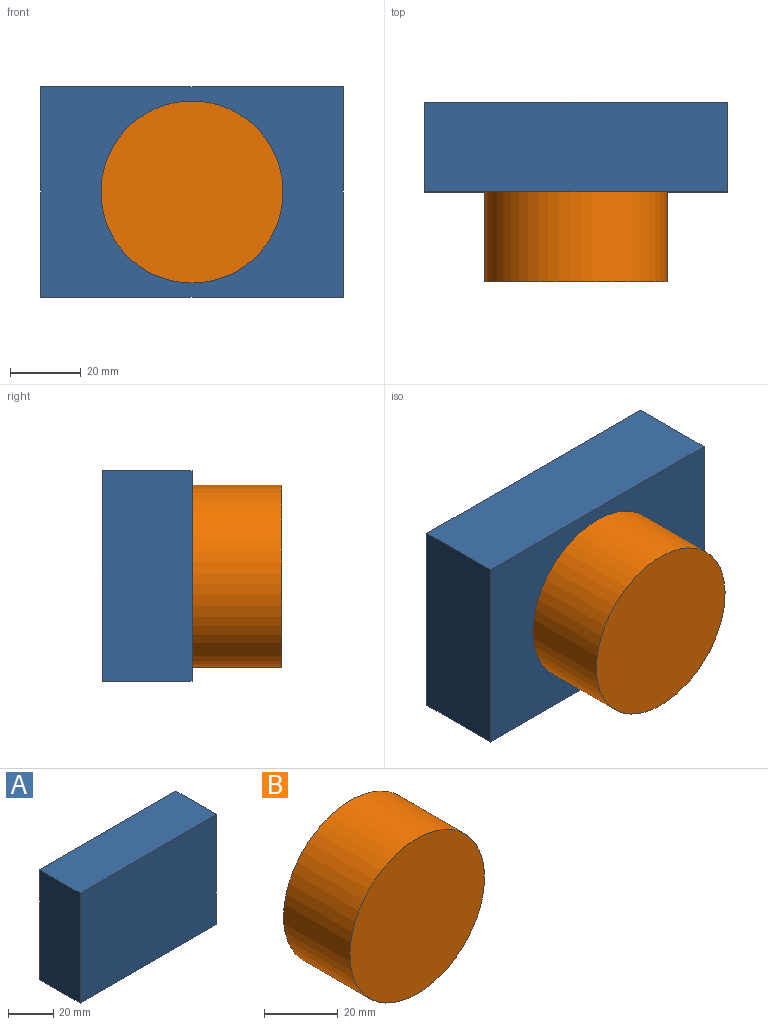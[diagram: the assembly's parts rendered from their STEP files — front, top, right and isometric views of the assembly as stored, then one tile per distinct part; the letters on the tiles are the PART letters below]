
ASSEMBLY  parts=2 mates=1
PART A: 6 faces, bbox 85.5x25.4x59.6 mm
  f0: plane 59.59x25.4mm, normal (-1,0,0), area 1513.6mm2, adj f1,f3,f4,f5
  f1: plane 85.46x25.4mm, normal (0,0,-1), area 2170.6mm2, adj f0,f2,f4,f5
  f2: plane 59.59x25.4mm, normal (1,0,0), area 1513.6mm2, adj f1,f3,f4,f5
  f3: plane 85.46x25.4mm, normal (0,0,1), area 2170.6mm2, adj f0,f2,f4,f5
  f4: plane 85.46x59.59mm, normal (0,-1,0), area 5092.2mm2, adj f0,f1,f2,f3
  f5: plane 85.46x59.59mm, normal (0,1,0), area 5092.2mm2, adj f0,f1,f2,f3
PART B: 3 faces, bbox 51.5x25.4x51.5 mm
  f0: cylinder r=25.76mm len=51.51mm, axis (0,1,0), area 4110.5mm2, adj f1,f2
  f1: plane 51.51x51.51mm, normal (0,-1,0), area 2084.1mm2, adj f0
  f2: plane 51.51x51.51mm, normal (0,1,0), area 2084.1mm2, adj f0
PLACE A t=(-52.41,-28.16,-23.63)mm
PLACE B t=(-9.68,-53.56,6.16)mm
MATE planar A.f4 <-> B.f0  axis (0,-1,0) through (-9.68,-53.56,6.16)mm
